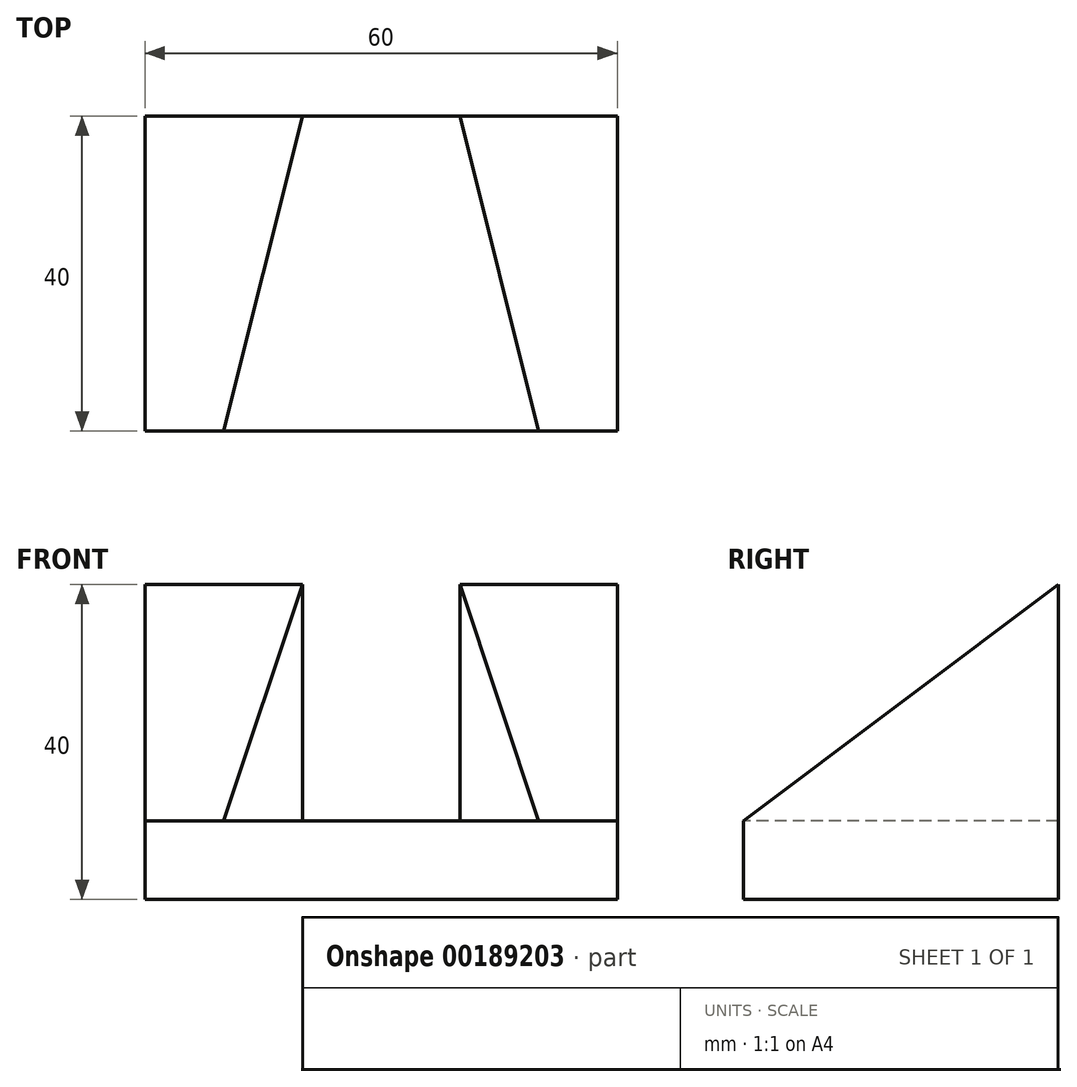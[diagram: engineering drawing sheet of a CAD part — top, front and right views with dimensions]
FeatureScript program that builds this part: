
annotation { "Feature Type Name" : "Feature", "Feature Type Description" : "" }
export const myFeature = defineFeature(function(context is Context, id is Id, definition is map)
    precondition{}
    {
        {
            var Q0;
            Q0=qCreatedBy(makeId("Right.planeOp"),FACE);
            var sketch = newSketch(context, id + "F0", { "sketchPlane" : qUnion([Q0])});
            skLineSegment(sketch, "E0.bottom", {"start": v(0, 0) * mm, "end": v(40, 0) * mm});
            skLineSegment(sketch, "E0.left", {"start": v(0, 0) * mm, "end": v(0, 10) * mm});
            skLineSegment(sketch, "E0.right", {"start": v(40, 0) * mm, "end": v(40, 40) * mm});
            skLineSegment(sketch, "E1", {"start": v(40, 40) * mm, "end": v(0, 10) * mm});
            skSolve(sketch);
        }
        {
            var Q0;
            Q0=makeQuery(id+"F0.imprint","IMPRINT",FACE,{"disambiguationData":[TD([[makeQuery(id+"F0.imprint","IMPRINT",EDGE,{"derivedFrom":sQuery(id+"F0.wireOp",EDGE,"E0.bottom")}),1.0]])]});
            extrude(context, id + "F1", {"entities" : qUnion([Q0]), "endBound" : BoundingType.SYMMETRIC, "depth" : 60 * mm});
        }
        {
            var Q0;
            Q0=qCreatedBy(makeId("Top.planeOp"),FACE);
            var Q1;
            Q1=makeQuery(id+"F1.opExtrude","SWEPT_EDGE",EDGE,{"disambiguationData":[OSD([sQuery(id+"F0.wireOp",EDGE,"E0.right"),sQuery(id+"F0.wireOp",EDGE,"E1")])]});
            cPlane(context, id + "F2", {"entities" : qUnion([Q0, Q1]), "cplaneType" : CPlaneType.LINE_ANGLE, "offset" : 25 * mm, "angle" : 0 * degree, "width" : 150 * mm, "height" : 150 * mm});
        }
        {
            var Q0;
            Q0=qCreatedBy(id+"F2.planeOp",FACE);
            var sketch = newSketch(context, id + "F3", { "sketchPlane" : qUnion([Q0])});
            skLineSegment(sketch, "E2", {"start": v(-10, -40) * mm, "end": v(-20, 0) * mm});
            skLineSegment(sketch, "E3", {"start": v(0, -40.46) * mm, "end": v(0, 0) * mm, "construction": true});
            skLineSegment(sketch, "E4.MirrorCS", {"start": v(10, -40) * mm, "end": v(20, 0) * mm});
            skLineSegment(sketch, "E5.0", {"start": v(10, -40) * mm, "end": v(-10, -40) * mm});
            skLineSegment(sketch, "E6.0", {"start": v(20, 0) * mm, "end": v(-20, 0) * mm});
            skPoint(sketch, "E7.orphan", {"position": v(-30, -40) * mm});
            skPoint(sketch, "E8.orphan", {"position": v(30, -40) * mm});
            skPoint(sketch, "E9.orphan", {"position": v(30, 0) * mm});
            skPoint(sketch, "E10.orphan", {"position": v(-30, 0) * mm});
            skSolve(sketch);
        }
        {
            var Q0;
            Q0=makeQuery(id+"F3.imprint","IMPRINT",FACE,{"disambiguationData":[TD([[makeQuery(id+"F3.imprint","IMPRINT",EDGE,{"derivedFrom":sQuery(id+"F3.wireOp",EDGE,"E2")}),-1.0]])]});
            extrude(context, id + "F4", {"entities" : qUnion([Q0]), "operationType" : NewBodyOperationType.REMOVE, "depth" : 30 * mm});
        }
    });
